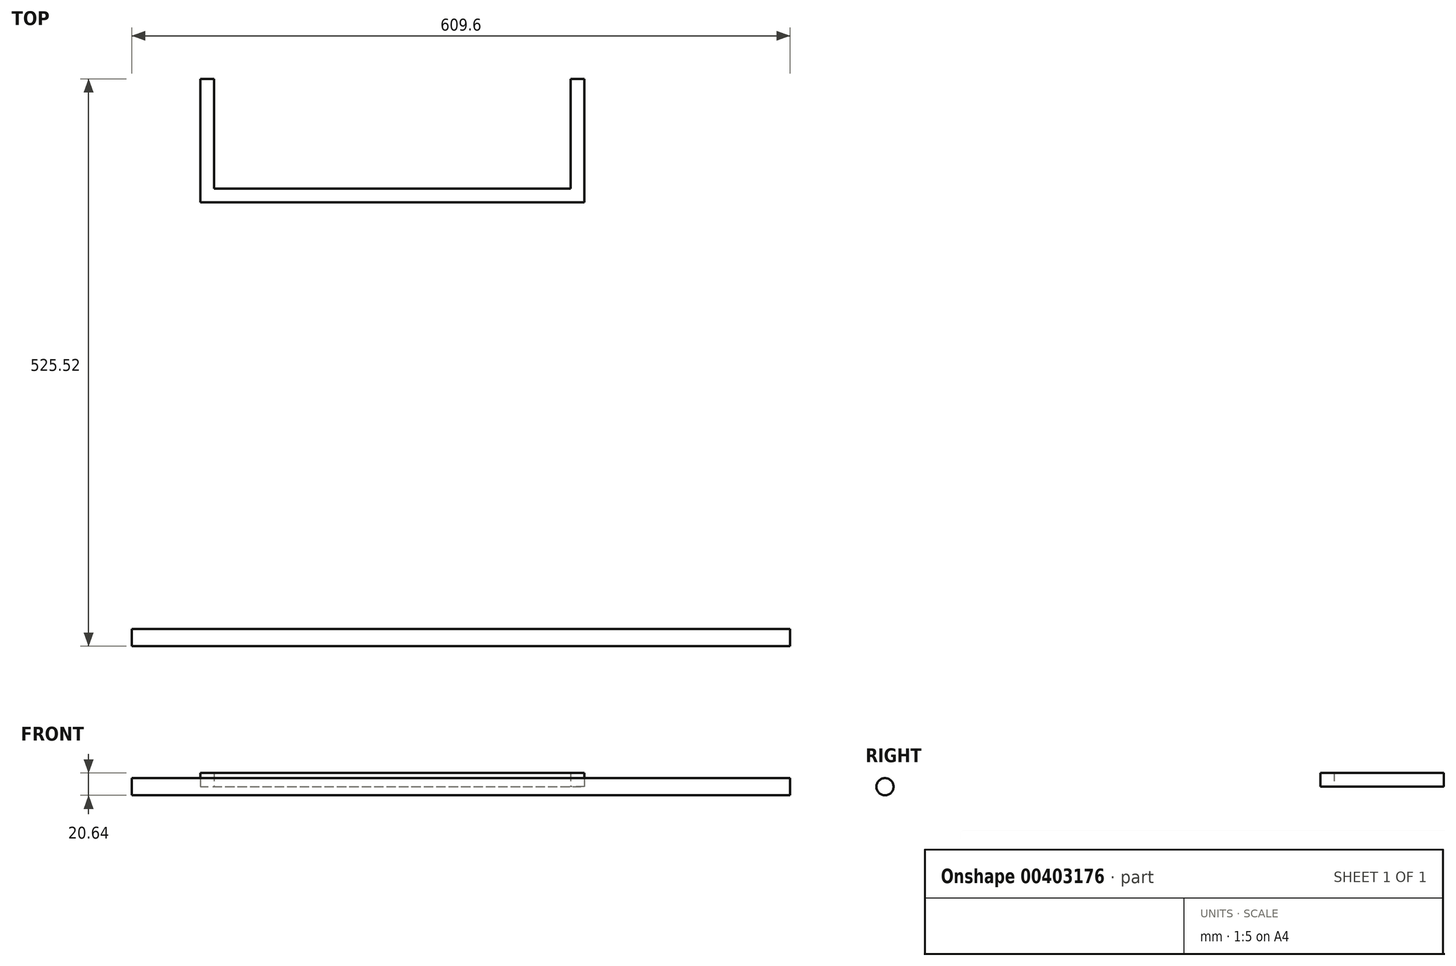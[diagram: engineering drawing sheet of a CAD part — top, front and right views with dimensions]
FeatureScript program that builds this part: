
annotation { "Feature Type Name" : "Feature", "Feature Type Description" : "" }
export const myFeature = defineFeature(function(context is Context, id is Id, definition is map)
    precondition{}
    {
        {
            var Q0;
            Q0=qCreatedBy(makeId("Top.planeOp"),FACE);
            var sketch = newSketch(context, id + "F0", { "sketchPlane" : qUnion([Q0])});
            skLineSegment(sketch, "E0", {"start": v(-304.8, 0) * mm, "end": v(304.8, 0) * mm});
            skLineSegment(sketch, "E1", {"start": v(-304.8, 0) * mm, "end": v(-304.8, 7.94) * mm});
            skLineSegment(sketch, "E2.MirrorCS", {"start": v(304.8, 0) * mm, "end": v(304.8, 7.94) * mm});
            skLineSegment(sketch, "E3", {"start": v(304.8, 7.94) * mm, "end": v(-304.8, 7.94) * mm});
            skSolve(sketch);
        }
        {
            var Q0;
            Q0=makeQuery(id+"F0.imprint","IMPRINT",FACE,{"disambiguationData":[TD([[makeQuery(id+"F0.imprint","IMPRINT",EDGE,{"derivedFrom":sQuery(id+"F0.wireOp",EDGE,"E0")}),1.0]])]});
            var Q1;
            Q1=sQuery(id+"F0.wireOp",EDGE,"E0");
            revolve(context, id + "F1", {"entities" : qUnion([Q0]), "axis" : qUnion([Q1]), "revolveType" : RevolveType.FULL});
        }
        {
            var Q0;
            Q0=qCreatedBy(makeId("Top.planeOp"),FACE);
            var sketch = newSketch(context, id + "F2", { "sketchPlane" : qUnion([Q0])});
            skLineSegment(sketch, "E4.bottom", {"start": v(-241.35, 517.58) * mm, "end": v(-228.65, 517.58) * mm});
            skLineSegment(sketch, "E4.left", {"start": v(-241.35, 517.58) * mm, "end": v(-241.35, 415.98) * mm});
            skLineSegment(sketch, "E4.right", {"start": v(-228.65, 517.58) * mm, "end": v(-228.65, 517.58) * mm});
            skLineSegment(sketch, "E5.top", {"start": v(-241.35, 403.28) * mm, "end": v(114.25, 403.28) * mm});
            skLineSegment(sketch, "E5.left", {"start": v(-241.35, 415.98) * mm, "end": v(-241.35, 403.28) * mm});
            skLineSegment(sketch, "E5.right", {"start": v(114.25, 517.58) * mm, "end": v(114.25, 403.28) * mm});
            skLineSegment(sketch, "E6", {"start": v(-228.65, 415.98) * mm, "end": v(101.55, 415.98) * mm});
            skLineSegment(sketch, "E7", {"start": v(-228.65, 517.58) * mm, "end": v(-228.65, 415.98) * mm});
            skLineSegment(sketch, "E8", {"start": v(114.25, 517.58) * mm, "end": v(101.55, 517.58) * mm});
            skLineSegment(sketch, "E9", {"start": v(101.55, 517.58) * mm, "end": v(101.55, 415.98) * mm});
            skSolve(sketch);
        }
        {
            var Q0;
            Q0 = qSketchRegion(id + "F2", true);
            extrude(context, id + "F3", {"entities" : qUnion([Q0]), "depth" : 12.7 * mm});
        }
    });
